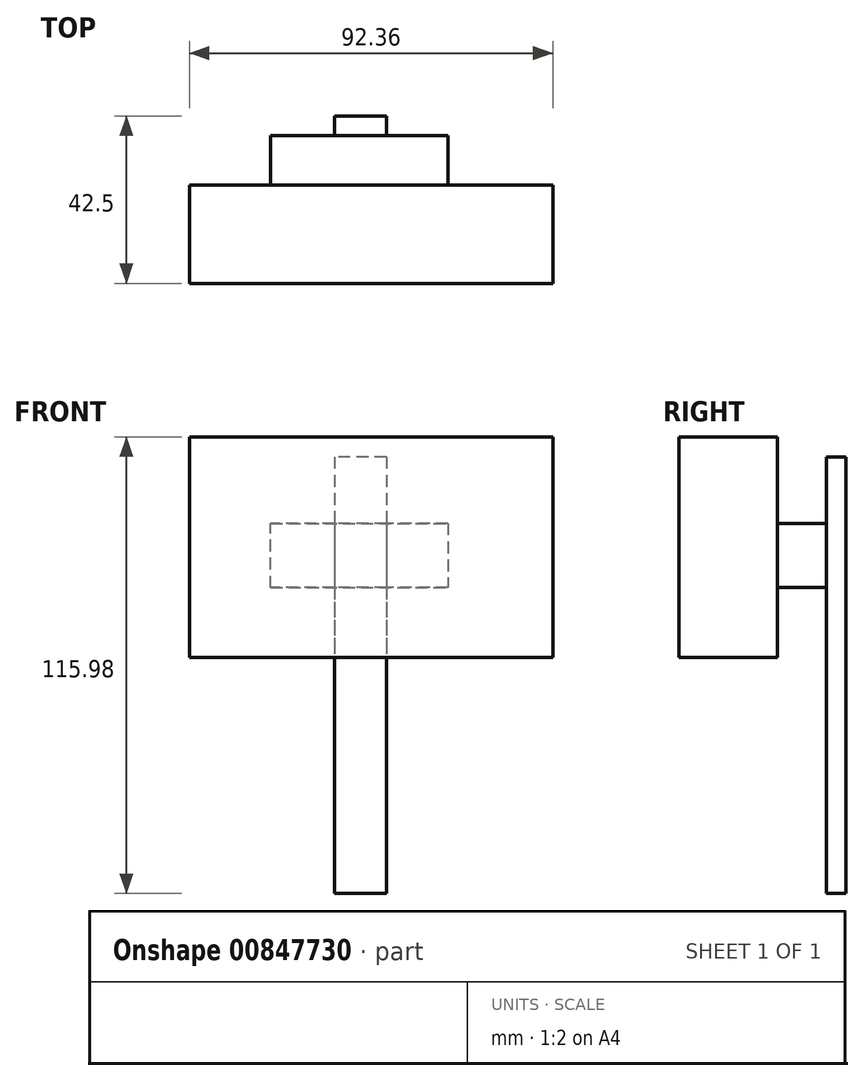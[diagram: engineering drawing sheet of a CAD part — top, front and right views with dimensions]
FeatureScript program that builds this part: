
annotation { "Feature Type Name" : "Feature", "Feature Type Description" : "" }
export const myFeature = defineFeature(function(context is Context, id is Id, definition is map)
    precondition{}
    {
        {
            var Q0;
            Q0=qCreatedBy(makeId("Front.planeOp"),FACE);
            var sketch = newSketch(context, id + "F0", { "sketchPlane" : qUnion([Q0])});
            skLineSegment(sketch, "E0.bottom", {"start": v(-43.28, 36.93) * mm, "end": v(49.08, 36.93) * mm});
            skLineSegment(sketch, "E0.top", {"start": v(-43.28, -19.14) * mm, "end": v(49.08, -19.14) * mm});
            skLineSegment(sketch, "E0.left", {"start": v(-43.28, 36.93) * mm, "end": v(-43.28, -19.14) * mm});
            skLineSegment(sketch, "E0.right", {"start": v(49.08, 36.93) * mm, "end": v(49.08, -19.14) * mm});
            skSolve(sketch);
        }
        {
            var Q0;
            Q0=makeQuery(id+"F0.imprint","IMPRINT",FACE,{"disambiguationData":[TD([[makeQuery(id+"F0.imprint","IMPRINT",EDGE,{"derivedFrom":sQuery(id+"F0.wireOp",EDGE,"E0.bottom")}),-1.0]])]});
            extrude(context, id + "F1", {"entities" : qUnion([Q0]), "depth" : 25 * mm, "offsetDistance" : 25 * mm});
        }
        {
            var Q0;
            Q0=qCreatedBy(makeId("Front.planeOp"),FACE);
            var sketch = newSketch(context, id + "F2", { "sketchPlane" : qUnion([Q0])});
            skLineSegment(sketch, "E1.bottom", {"start": v(22.4, 14.97) * mm, "end": v(-22.6, 14.97) * mm});
            skLineSegment(sketch, "E1.top", {"start": v(22.4, -1.36) * mm, "end": v(-22.6, -1.36) * mm});
            skLineSegment(sketch, "E1.left", {"start": v(22.4, 14.97) * mm, "end": v(22.4, -1.36) * mm});
            skLineSegment(sketch, "E1.right", {"start": v(-22.6, 14.97) * mm, "end": v(-22.6, -1.36) * mm});
            skSolve(sketch);
        }
        {
            var Q0;
            Q0=makeQuery(id+"F2.imprint","IMPRINT",FACE,{"disambiguationData":[TD([[makeQuery(id+"F2.imprint","IMPRINT",EDGE,{"derivedFrom":sQuery(id+"F2.wireOp",EDGE,"E1.bottom")}),1.0]])]});
            extrude(context, id + "F3", {"entities" : qUnion([Q0]), "operationType" : NewBodyOperationType.ADD, "endBound" : BoundingType.SYMMETRIC, "depth" : 25 * mm, "offsetDistance" : 25 * mm});
        }
        {
            var Q0;
            Q0=makeQuery(id+"F3.opExtrude","CAP_FACE",FACE,{"disambiguationData":[OSD([sQuery(id+"F2.wireOp",EDGE,"E1.bottom"),sQuery(id+"F2.wireOp",EDGE,"E1.top"),sQuery(id+"F2.wireOp",EDGE,"E1.left"),sQuery(id+"F2.wireOp",EDGE,"E1.right")])],"isStart":true});
            var sketch = newSketch(context, id + "F4", { "sketchPlane" : qUnion([Q0])});
            skSolve(sketch);
        }
        {
            var Q0;
            Q0=makeQuery(id+"F4.imprint","IMPRINT",FACE,{"disambiguationData":[TD([[makeQuery(id+"F4.imprint","IMPRINT",EDGE,{"derivedFrom":makeQuery(id+"F3.opExtrude","CAP_EDGE",EDGE,{"disambiguationData":[OSD([sQuery(id+"F2.wireOp",EDGE,"E1.bottom")])],"isStart":true})}),-1.0]])]});
            var sketch = newSketch(context, id + "F5", { "sketchPlane" : qUnion([Q0])});
            skLineSegment(sketch, "E2.bottom", {"start": v(-6.8, 31.84) * mm, "end": v(6.45, 31.84) * mm});
            skLineSegment(sketch, "E2.top", {"start": v(-6.8, -79.05) * mm, "end": v(6.45, -79.05) * mm});
            skLineSegment(sketch, "E2.left", {"start": v(-6.8, 31.84) * mm, "end": v(-6.8, -79.05) * mm});
            skLineSegment(sketch, "E2.right", {"start": v(6.45, 31.84) * mm, "end": v(6.45, -79.05) * mm});
            skSolve(sketch);
        }
        {
            var Q0;
            {var subQ0=sQuery(id+"F5.wireOp",EDGE,"E2.bottom");Q0=makeQuery(id+"F5.imprint","IMPRINT",FACE,{"disambiguationData":[TD([[makeQuery(id+"F5.imprint","IMPRINT",EDGE,{"derivedFrom":subQ0}),-1.0]])]});}
            var Q1;
            {var subQ0=sQuery(id+"F5.wireOp",EDGE,"E2.left");var subQ1=makeQuery(id+"F4.imprint","IMPRINT",EDGE,{"derivedFrom":makeQuery(id+"F3.opExtrude","CAP_EDGE",EDGE,{"disambiguationData":[OSD([sQuery(id+"F2.wireOp",EDGE,"E1.bottom")])],"isStart":true})});var subQ2=makeQuery(id+"F5.imprint","INTERSECT",VERTEX,{"derivedFrom":[subQ1,subQ0]});Q1=makeQuery(id+"F5.imprint","IMPRINT",FACE,{"disambiguationData":[TD([[makeQuery(id+"F5.imprint","IMPRINT",EDGE,{"disambiguationData":[TD([[subQ2,-1.0]])],"derivedFrom":subQ0}),1.0]])]});}
            var Q2;
            {var subQ0=sQuery(id+"F5.wireOp",EDGE,"E2.top");Q2=makeQuery(id+"F5.imprint","IMPRINT",FACE,{"disambiguationData":[TD([[makeQuery(id+"F5.imprint","IMPRINT",EDGE,{"derivedFrom":subQ0}),1.0]])]});}
            extrude(context, id + "F6", {"entities" : qUnion([Q0, Q1, Q2]), "operationType" : NewBodyOperationType.ADD, "depth" : 5 * mm, "offsetDistance" : 25 * mm});
        }
        {
            var Q0;
            Q0=makeQuery(id+"F6.opExtrude","SWEPT_FACE",FACE,{"disambiguationData":[OSD([sQuery(id+"F5.wireOp",EDGE,"E2.top")])]});
            var sketch = newSketch(context, id + "F7", { "sketchPlane" : qUnion([Q0])});
            skSolve(sketch);
        }
        {
            var Q0;
            {var subQ0=sQuery(id+"F5.wireOp",EDGE,"E2.top");Q0=makeQuery(id+"F7.imprint","IMPRINT",FACE,{"disambiguationData":[TD([[makeQuery(id+"F7.imprint","IMPRINT",EDGE,{"derivedFrom":makeQuery(id+"F6.opExtrude","CAP_EDGE",EDGE,{"disambiguationData":[OSD([subQ0])],"isStart":true})}),1.0]])]});}
            var sketch = newSketch(context, id + "F8", { "sketchPlane" : qUnion([Q0])});
            skSolve(sketch);
        }
        {
            var Q0;
            {var subQ0=sQuery(id+"F5.wireOp",EDGE,"E2.top");Q0=makeQuery(id+"F8.imprint","IMPRINT",FACE,{"disambiguationData":[TD([[makeQuery(id+"F8.imprint","IMPRINT",EDGE,{"derivedFrom":makeQuery(id+"F7.imprint","IMPRINT",EDGE,{"derivedFrom":makeQuery(id+"F6.opExtrude","CAP_EDGE",EDGE,{"disambiguationData":[OSD([subQ0])],"isStart":true})})}),1.0]])]});}
            var sketch = newSketch(context, id + "F9", { "sketchPlane" : qUnion([Q0])});
            skArc(sketch, "E3", {"start": v(55.61, -41.28) * mm, "mid": v(2.92, -14.44) * mm, "end": v(-51.08, -38.56) * mm});
            skSolve(sketch);
        }
    });
